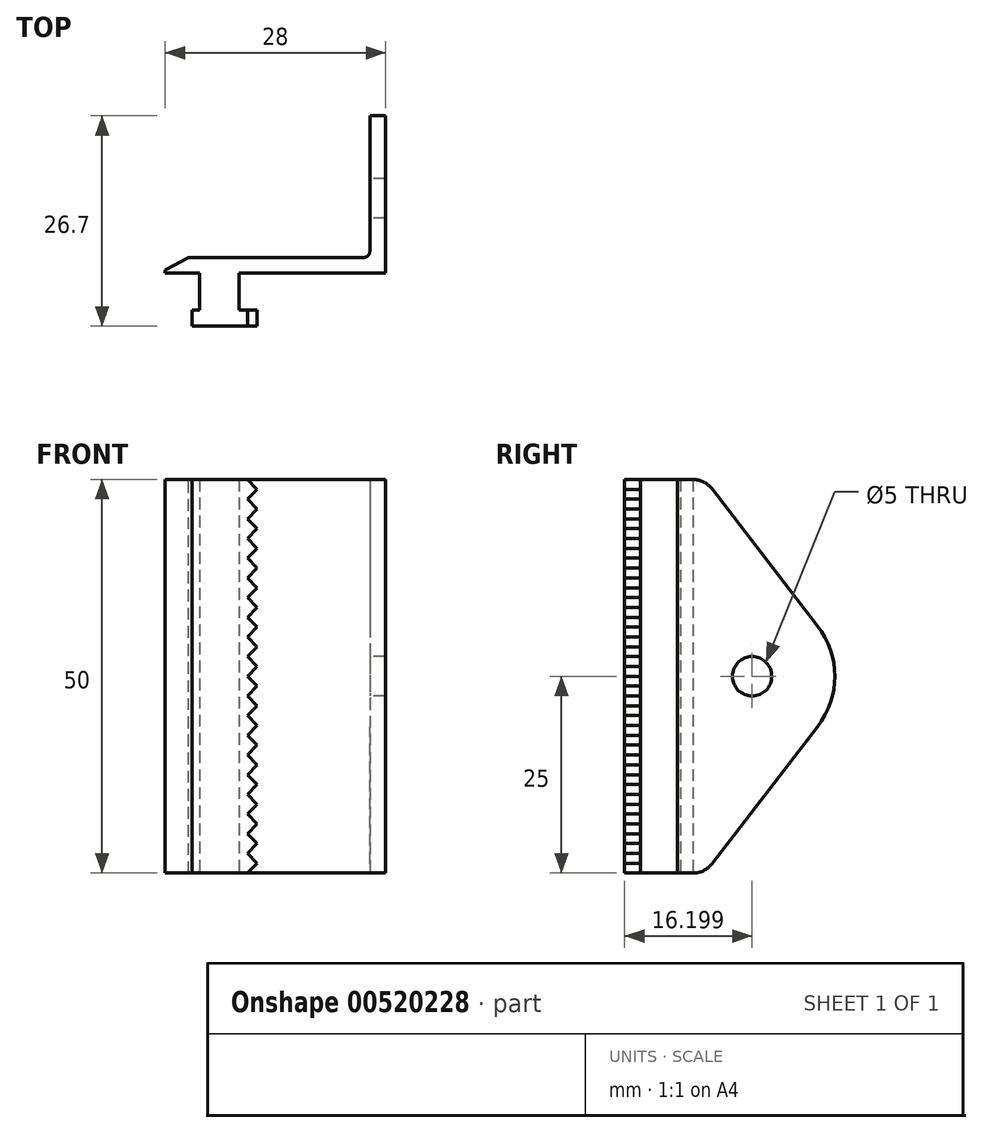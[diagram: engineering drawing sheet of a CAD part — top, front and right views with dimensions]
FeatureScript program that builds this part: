
annotation { "Feature Type Name" : "Feature", "Feature Type Description" : "" }
export const myFeature = defineFeature(function(context is Context, id is Id, definition is map)
    precondition{}
    {
        {
            var Q0;
            Q0=qCreatedBy(makeId("Top.planeOp"),FACE);
            var sketch = newSketch(context, id + "F0", { "sketchPlane" : qUnion([Q0])});
            skLineSegment(sketch, "E0", {"start": v(17.42, -14.47) * mm, "end": v(17.42, 3.53) * mm});
            skLineSegment(sketch, "E1", {"start": v(17.42, 3.53) * mm, "end": v(19.42, 3.53) * mm});
            skLineSegment(sketch, "E2", {"start": v(19.42, 3.53) * mm, "end": v(19.42, -16.47) * mm});
            skLineSegment(sketch, "E3", {"start": v(19.42, -16.47) * mm, "end": v(0.82, -16.47) * mm});
            skLineSegment(sketch, "E4", {"start": v(0.82, -16.47) * mm, "end": v(0.82, -21.17) * mm});
            skLineSegment(sketch, "E5", {"start": v(0.82, -21.17) * mm, "end": v(3.12, -21.17) * mm});
            skLineSegment(sketch, "E6", {"start": v(3.12, -21.17) * mm, "end": v(3.12, -23.17) * mm});
            skLineSegment(sketch, "E7", {"start": v(3.12, -23.17) * mm, "end": v(-5.18, -23.17) * mm});
            skLineSegment(sketch, "E8", {"start": v(-5.18, -23.17) * mm, "end": v(-5.18, -21.17) * mm});
            skLineSegment(sketch, "E9", {"start": v(-5.18, -21.17) * mm, "end": v(-4.18, -21.17) * mm});
            skLineSegment(sketch, "E10", {"start": v(-4.18, -21.17) * mm, "end": v(-4.18, -16.47) * mm});
            skLineSegment(sketch, "E11", {"start": v(-4.18, -16.47) * mm, "end": v(-8.58, -16.47) * mm});
            skLineSegment(sketch, "E12", {"start": v(-8.58, -16.47) * mm, "end": v(-8.58, -14.47) * mm});
            skLineSegment(sketch, "E13", {"start": v(-8.58, -14.47) * mm, "end": v(17.42, -14.47) * mm});
            skSolve(sketch);
        }
        {
            var Q0;
            Q0 = qSketchRegion(id + "F0", true);
            extrude(context, id + "F1", {"entities" : qUnion([Q0]), "depth" : 50 * mm, "offsetDistance" : 25 * mm});
        }
        {
            var Q0;
            Q0=makeQuery(id+"F1.opExtrude","SWEPT_FACE",FACE,{"disambiguationData":[OSD([sQuery(id+"F0.wireOp",EDGE,"E0")])]});
            var sketch = newSketch(context, id + "F2", { "sketchPlane" : qUnion([Q0])});
            skCircle(sketch, "E14", {"center": v(6.97, 25) * mm, "radius": 2.5 * mm});
            skLineSegment(sketch, "E15", {"start": v(-13.38, -16.28) * mm, "end": v(-13.38, 56.69) * mm});
            skArc(sketch, "E16", {"start": v(-1.34, 18.59) * mm, "mid": v(-3.53, 25.02) * mm, "end": v(-1.32, 31.45) * mm});
            skLineSegment(sketch, "E17", {"start": v(12.1, 1.17) * mm, "end": v(-1.34, 18.59) * mm});
            skArc(sketch, "E18", {"start": v(14.47, 0) * mm, "mid": v(13.15, 0.3) * mm, "end": v(12.1, 1.17) * mm});
            skLineSegment(sketch, "E19", {"start": v(6.97, 25) * mm, "end": v(2.56, 25) * mm, "construction": true});
            skArc(sketch, "E20.MirrorCS", {"start": v(14.47, 50) * mm, "mid": v(13.15, 49.7) * mm, "end": v(12.1, 48.83) * mm});
            skLineSegment(sketch, "E21.MirrorCS", {"start": v(12.1, 48.83) * mm, "end": v(-1.34, 31.41) * mm});
            skLineSegment(sketch, "E22", {"start": v(14.47, 0) * mm, "end": v(14.47, -1.73) * mm});
            skLineSegment(sketch, "E23", {"start": v(14.47, -1.73) * mm, "end": v(-4.85, -2.1) * mm});
            skLineSegment(sketch, "E24", {"start": v(-4.85, -2.1) * mm, "end": v(-5.91, 53.22) * mm});
            skLineSegment(sketch, "E25", {"start": v(-5.91, 53.22) * mm, "end": v(14.47, 50.8) * mm});
            skLineSegment(sketch, "E26", {"start": v(14.47, 50.8) * mm, "end": v(14.47, 50) * mm});
            skSolve(sketch);
        }
        {
            var Q0;
            Q0 = qSketchRegion(id + "F2", true);
            extrude(context, id + "F3", {"entities" : qUnion([Q0]), "operationType" : NewBodyOperationType.REMOVE, "endBound" : BoundingType.THROUGH_ALL, "oppositeDirection" : true, "depth" : 25 * mm, "offsetDistance" : 25 * mm});
        }
        {
            var Q0;
            Q0=makeQuery(id+"F1.opExtrude","SWEPT_FACE",FACE,{"disambiguationData":[OSD([sQuery(id+"F0.wireOp",EDGE,"E7")])]});
            var sketch = newSketch(context, id + "F4", { "sketchPlane" : qUnion([Q0])});
            skLineSegment(sketch, "E27", {"start": v(1.87, 50) * mm, "end": v(3.12, 48.75) * mm});
            skLineSegment(sketch, "E28", {"start": v(3.12, 48.75) * mm, "end": v(1.87, 47.5) * mm});
            skLineSegment(sketch, "E29.0.1.0", {"start": v(1.87, 47.5) * mm, "end": v(3.12, 46.25) * mm});
            skLineSegment(sketch, "E29.0.1.1", {"start": v(3.12, 46.25) * mm, "end": v(1.87, 45) * mm});
            skLineSegment(sketch, "E29.0.2.0", {"start": v(1.87, 45) * mm, "end": v(3.12, 43.75) * mm});
            skLineSegment(sketch, "E29.0.2.1", {"start": v(3.12, 43.75) * mm, "end": v(1.87, 42.5) * mm});
            skLineSegment(sketch, "E29.0.3.0", {"start": v(1.87, 42.5) * mm, "end": v(3.12, 41.25) * mm});
            skLineSegment(sketch, "E29.0.3.1", {"start": v(3.12, 41.25) * mm, "end": v(1.87, 40) * mm});
            skLineSegment(sketch, "E29.0.4.0", {"start": v(1.87, 40) * mm, "end": v(3.12, 38.75) * mm});
            skLineSegment(sketch, "E29.0.4.1", {"start": v(3.12, 38.75) * mm, "end": v(1.87, 37.5) * mm});
            skLineSegment(sketch, "E29.0.5.0", {"start": v(1.87, 37.5) * mm, "end": v(3.12, 36.25) * mm});
            skLineSegment(sketch, "E29.0.5.1", {"start": v(3.12, 36.25) * mm, "end": v(1.87, 35) * mm});
            skLineSegment(sketch, "E29.0.6.0", {"start": v(1.87, 35) * mm, "end": v(3.12, 33.75) * mm});
            skLineSegment(sketch, "E29.0.6.1", {"start": v(3.12, 33.75) * mm, "end": v(1.87, 32.5) * mm});
            skLineSegment(sketch, "E29.0.7.0", {"start": v(1.87, 32.5) * mm, "end": v(3.12, 31.25) * mm});
            skLineSegment(sketch, "E29.0.7.1", {"start": v(3.12, 31.25) * mm, "end": v(1.87, 30) * mm});
            skLineSegment(sketch, "E29.0.8.0", {"start": v(1.87, 30) * mm, "end": v(3.12, 28.75) * mm});
            skLineSegment(sketch, "E29.0.8.1", {"start": v(3.12, 28.75) * mm, "end": v(1.87, 27.5) * mm});
            skLineSegment(sketch, "E29.0.9.0", {"start": v(1.87, 27.5) * mm, "end": v(3.12, 26.25) * mm});
            skLineSegment(sketch, "E29.0.9.1", {"start": v(3.12, 26.25) * mm, "end": v(1.87, 25) * mm});
            skLineSegment(sketch, "E29.0.10.0", {"start": v(1.87, 25) * mm, "end": v(3.12, 23.75) * mm});
            skLineSegment(sketch, "E29.0.10.1", {"start": v(3.12, 23.75) * mm, "end": v(1.87, 22.5) * mm});
            skLineSegment(sketch, "E29.0.11.0", {"start": v(1.87, 22.5) * mm, "end": v(3.12, 21.25) * mm});
            skLineSegment(sketch, "E29.0.11.1", {"start": v(3.12, 21.25) * mm, "end": v(1.87, 20) * mm});
            skLineSegment(sketch, "E29.0.12.0", {"start": v(1.87, 20) * mm, "end": v(3.12, 18.75) * mm});
            skLineSegment(sketch, "E29.0.12.1", {"start": v(3.12, 18.75) * mm, "end": v(1.87, 17.5) * mm});
            skLineSegment(sketch, "E29.0.13.0", {"start": v(1.87, 17.5) * mm, "end": v(3.12, 16.25) * mm});
            skLineSegment(sketch, "E29.0.13.1", {"start": v(3.12, 16.25) * mm, "end": v(1.87, 15) * mm});
            skLineSegment(sketch, "E29.0.14.0", {"start": v(1.87, 15) * mm, "end": v(3.12, 13.75) * mm});
            skLineSegment(sketch, "E29.0.14.1", {"start": v(3.12, 13.75) * mm, "end": v(1.87, 12.5) * mm});
            skLineSegment(sketch, "E29.0.15.0", {"start": v(1.87, 12.5) * mm, "end": v(3.12, 11.25) * mm});
            skLineSegment(sketch, "E29.0.15.1", {"start": v(3.12, 11.25) * mm, "end": v(1.87, 10) * mm});
            skLineSegment(sketch, "E29.0.16.0", {"start": v(1.87, 10) * mm, "end": v(3.12, 8.75) * mm});
            skLineSegment(sketch, "E29.0.16.1", {"start": v(3.12, 8.75) * mm, "end": v(1.87, 7.5) * mm});
            skLineSegment(sketch, "E29.0.17.0", {"start": v(1.87, 7.5) * mm, "end": v(3.12, 6.25) * mm});
            skLineSegment(sketch, "E29.0.17.1", {"start": v(3.12, 6.25) * mm, "end": v(1.87, 5) * mm});
            skLineSegment(sketch, "E29.0.18.0", {"start": v(1.87, 5) * mm, "end": v(3.12, 3.75) * mm});
            skLineSegment(sketch, "E29.0.18.1", {"start": v(3.12, 3.75) * mm, "end": v(1.87, 2.5) * mm});
            skLineSegment(sketch, "E29.0.19.0", {"start": v(1.87, 2.5) * mm, "end": v(3.12, 1.25) * mm});
            skLineSegment(sketch, "E29.0.19.1", {"start": v(3.12, 1.25) * mm, "end": v(1.87, 0) * mm});
            skLineSegment(sketch, "E29.direction1", {"start": v(1.87, 47.5) * mm, "end": v(26.87, 47.5) * mm, "construction": true});
            skLineSegment(sketch, "E29.direction2", {"start": v(1.87, 47.5) * mm, "end": v(1.87, 45) * mm, "construction": true});
            skLineSegment(sketch, "E30", {"start": v(1.87, 50) * mm, "end": v(1.87, 53.75) * mm});
            skLineSegment(sketch, "E31", {"start": v(1.87, 53.75) * mm, "end": v(7.3, 53.75) * mm});
            skLineSegment(sketch, "E32", {"start": v(7.3, 53.75) * mm, "end": v(7.74, -2.06) * mm});
            skLineSegment(sketch, "E33", {"start": v(7.74, -2.06) * mm, "end": v(1.87, -2.1) * mm});
            skLineSegment(sketch, "E34", {"start": v(1.87, -2.1) * mm, "end": v(1.87, 0) * mm});
            skSolve(sketch);
        }
        {
            var Q0;
            Q0 = qSketchRegion(id + "F4", true);
            extrude(context, id + "F5", {"entities" : qUnion([Q0]), "operationType" : NewBodyOperationType.REMOVE, "oppositeDirection" : true, "depth" : 5 * mm, "offsetDistance" : 25 * mm});
        }
        {
            var Q0;
            Q0=makeQuery(id+"F3.boolean.opBoolean","COPY",EDGE,{"derivedFrom":makeQuery(id+"F3.opExtrude","CAP_EDGE",EDGE,{"disambiguationData":[OSD([sQuery(id+"F2.wireOp",EDGE,"H47rL1nx-PM4Z-u45E-wCSj-xxSC1GHMHHE0")])],"isStart":true})});
            var Q1;
            Q1=makeQuery(id+"F3.boolean.opBoolean","COPY",EDGE,{"derivedFrom":makeQuery(id+"F3.opExtrude","CAP_EDGE",EDGE,{"disambiguationData":[OSD([sQuery(id+"F2.wireOp",EDGE,"E16")])],"isStart":true})});
            var Q2;
            Q2=makeQuery(id+"F3.boolean.opBoolean","COPY",EDGE,{"derivedFrom":makeQuery(id+"F3.opExtrude","CAP_EDGE",EDGE,{"disambiguationData":[OSD([sQuery(id+"F2.wireOp",EDGE,"E17")])],"isStart":true})});
            var Q3;
            Q3=makeQuery(id+"F1.opExtrude","SWEPT_EDGE",EDGE,{"disambiguationData":[OSD([sQuery(id+"F0.wireOp",EDGE,"E12"),sQuery(id+"F0.wireOp",EDGE,"E13")])]});
            chamfer(context, id + "F6", {"entities" : qUnion([Q0, Q1, Q2, Q3]), "chamferType" : ChamferType.TWO_OFFSETS, "width1" : 1.6 * mm, "oppositeDirection" : false, "width2" : 3 * mm, "tangentPropagation" : true});
        }
        {
            var Q0;
            Q0=makeQuery(id+"F1.opExtrude","SWEPT_EDGE",EDGE,{"disambiguationData":[OSD([sQuery(id+"F0.wireOp",EDGE,"E0"),sQuery(id+"F0.wireOp",EDGE,"E13")])]});
            var Q1;
            Q1=makeQuery(id+"F6.opChamfer","BLEND_EDGE",EDGE,{"blendedFrom":[makeQuery(id+"F3.boolean.opBoolean","COPY",EDGE,{"derivedFrom":makeQuery(id+"F3.opExtrude","CAP_EDGE",EDGE,{"disambiguationData":[OSD([sQuery(id+"F2.wireOp",EDGE,"E17")])],"isStart":true})}),makeQuery(id+"F1.opExtrude","SWEPT_FACE",FACE,{"disambiguationData":[OSD([sQuery(id+"F0.wireOp",EDGE,"E13")])]})],"blendedInto":[makeQuery(id+"F1.opExtrude","SWEPT_FACE",FACE,{"disambiguationData":[OSD([sQuery(id+"F0.wireOp",EDGE,"E13")])]})]});
            var Q2;
            Q2=makeQuery(id+"F6.opChamfer","BLEND_EDGE",EDGE,{"blendedFrom":[makeQuery(id+"F3.boolean.opBoolean","COPY",EDGE,{"derivedFrom":makeQuery(id+"F3.opExtrude","CAP_EDGE",EDGE,{"disambiguationData":[OSD([sQuery(id+"F2.wireOp",EDGE,"H47rL1nx-PM4Z-u45E-wCSj-xxSC1GHMHHE0")])],"isStart":true})}),makeQuery(id+"F1.opExtrude","SWEPT_FACE",FACE,{"disambiguationData":[OSD([sQuery(id+"F0.wireOp",EDGE,"E13")])]})],"blendedInto":[makeQuery(id+"F1.opExtrude","SWEPT_FACE",FACE,{"disambiguationData":[OSD([sQuery(id+"F0.wireOp",EDGE,"E13")])]})]});
            var Q3;
            Q3=makeQuery(id+"F6.opChamfer","BLEND_EDGE",EDGE,{"blendedFrom":[makeQuery(id+"F3.boolean.opBoolean","COPY",EDGE,{"derivedFrom":makeQuery(id+"F3.opExtrude","CAP_EDGE",EDGE,{"disambiguationData":[OSD([sQuery(id+"F2.wireOp",EDGE,"E21.MirrorCS")])],"isStart":true})}),makeQuery(id+"F1.opExtrude","SWEPT_FACE",FACE,{"disambiguationData":[OSD([sQuery(id+"F0.wireOp",EDGE,"E13")])]})],"blendedInto":[makeQuery(id+"F1.opExtrude","SWEPT_FACE",FACE,{"disambiguationData":[OSD([sQuery(id+"F0.wireOp",EDGE,"E13")])]})]});
            fillet(context, id + "F7", {"entities" : qUnion([Q0, Q1, Q2, Q3]), "radius" : 0.8 * mm, "tangentPropagation" : true, "allowEdgeOverflow" : false});
        }
    });
